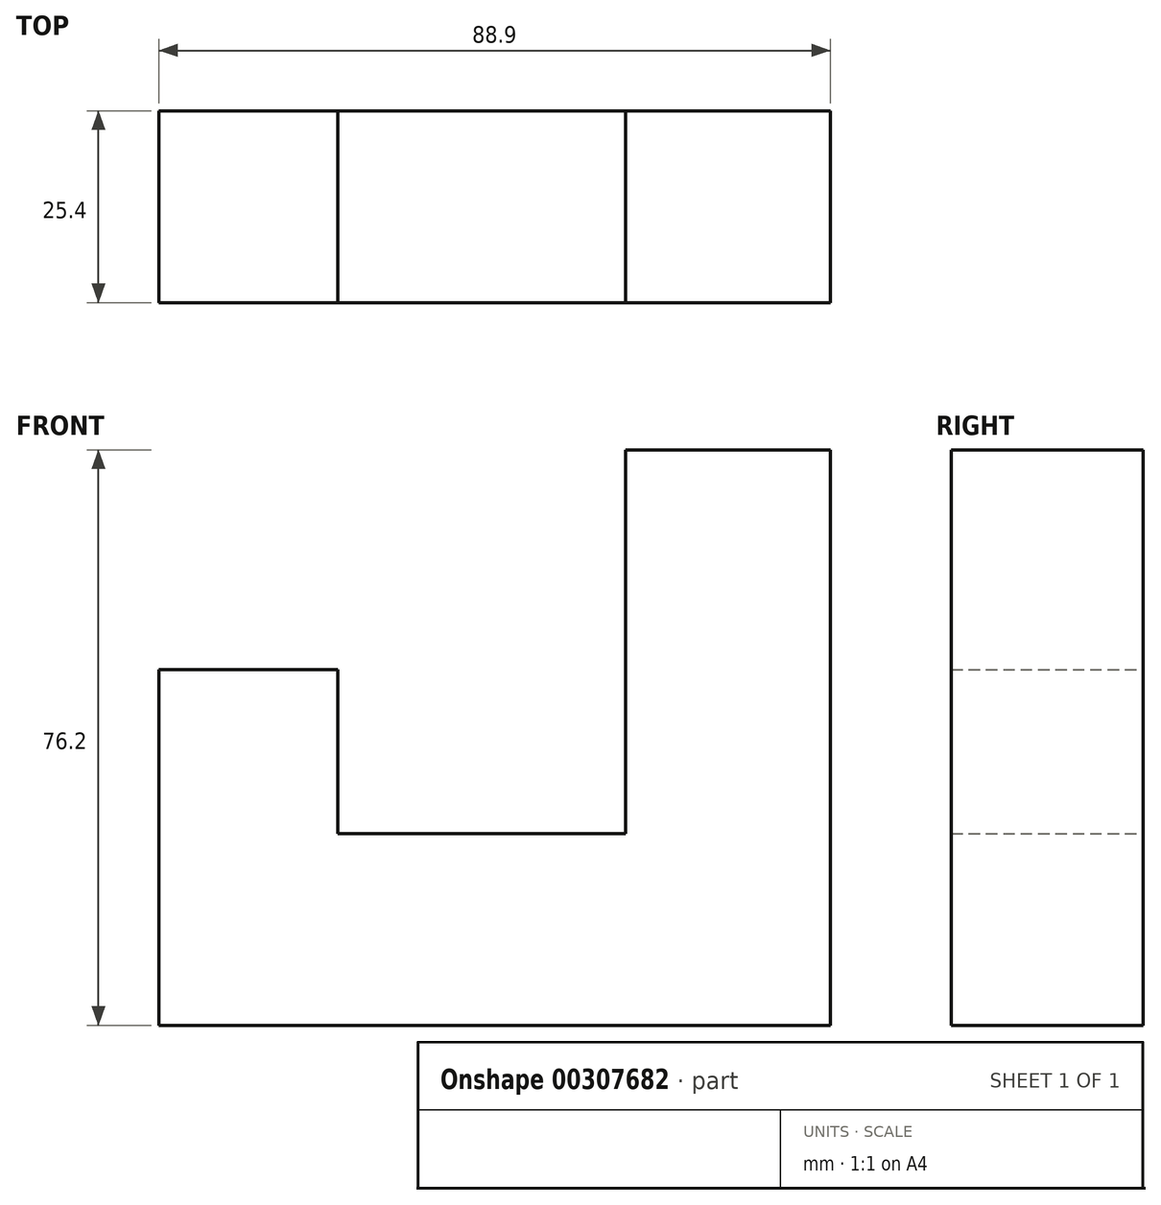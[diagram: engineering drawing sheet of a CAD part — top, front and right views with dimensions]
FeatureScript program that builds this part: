
annotation { "Feature Type Name" : "Feature", "Feature Type Description" : "" }
export const myFeature = defineFeature(function(context is Context, id is Id, definition is map)
    precondition{}
    {
        {
            var Q0;
            Q0=qCreatedBy(makeId("Front.planeOp"),FACE);
            var sketch = newSketch(context, id + "F0", { "sketchPlane" : qUnion([Q0])});
            skLineSegment(sketch, "E0", {"start": v(-30.02, -31.36) * mm, "end": v(46.18, -31.36) * mm});
            skLineSegment(sketch, "E1", {"start": v(46.18, -31.36) * mm, "end": v(46.18, 44.84) * mm});
            skLineSegment(sketch, "E2", {"start": v(46.18, 44.84) * mm, "end": v(19.04, 44.84) * mm});
            skLineSegment(sketch, "E3", {"start": v(19.04, 44.84) * mm, "end": v(19.04, -5.96) * mm});
            skLineSegment(sketch, "E4", {"start": v(19.04, -5.96) * mm, "end": v(-19.06, -5.96) * mm});
            skLineSegment(sketch, "E5", {"start": v(-19.06, -5.96) * mm, "end": v(-19.06, 15.75) * mm});
            skLineSegment(sketch, "E6", {"start": v(-19.06, 15.75) * mm, "end": v(-42.72, 15.75) * mm});
            skLineSegment(sketch, "E7", {"start": v(-42.72, 15.75) * mm, "end": v(-42.72, -31.36) * mm});
            skLineSegment(sketch, "E8", {"start": v(-42.72, -31.36) * mm, "end": v(-30.02, -31.36) * mm});
            skSolve(sketch);
        }
        {
            var Q0;
            Q0=makeQuery(id+"F0.imprint","IMPRINT",FACE,{"disambiguationData":[TD([[makeQuery(id+"F0.imprint","IMPRINT",EDGE,{"derivedFrom":sQuery(id+"F0.wireOp",EDGE,"E0")}),1.0]])]});
            extrude(context, id + "F1", {"entities" : qUnion([Q0]), "depth" : 25.4 * mm});
        }
    });
